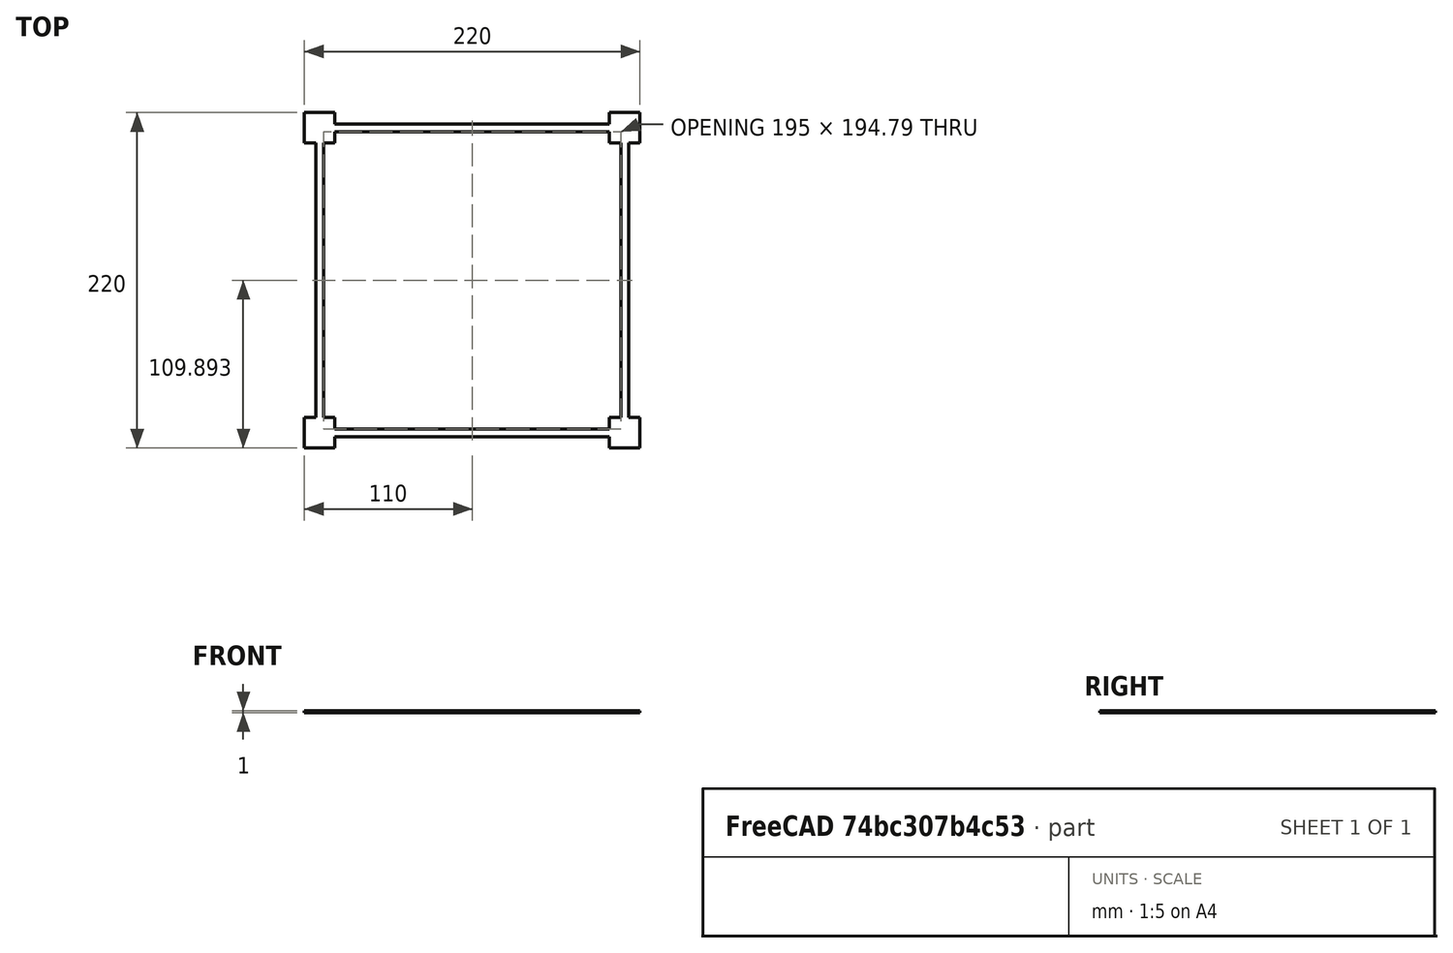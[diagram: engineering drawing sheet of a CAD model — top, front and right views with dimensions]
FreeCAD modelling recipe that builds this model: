
FCSTD DOCUMENT  (FreeCAD 1.1R42131 (Git))
Label: Ender 3 V3 SE Levelling
License: All rights reserved
LicenseURL: https://en.wikipedia.org/wiki/All_rights_reserved
objects: App::Point×1, Sketcher::SketchObject×1, PartDesign::Pad×1, PartDesign::Body×1
note: 6 computed .brp shape members not serialized (recipe doc carries the construction recipe); baked Part::Feature solids carry a one-line shape summary decoded from their .brp

FEATURE [App::Point] Origin001
  Role = Origin
FEATURE [Sketcher::SketchObject] Sketch
  ArcFitTolerance = 1e-06
  AttachmentSupport = -> [Origin]
  ExternalTypes = [0]
  FullyConstrained = false
  MakeInternals = false
  MapMode = 5
  sketch-geometry (36):
    g0: LineSegment StartX=-110 StartY=110 StartZ=0 EndX=-110 EndY=90 EndZ=0
    g1: LineSegment StartX=-110 StartY=90 StartZ=0 EndX=-90 EndY=90 EndZ=0
    g2: LineSegment StartX=-90 StartY=90 StartZ=0 EndX=-90 EndY=110 EndZ=0
    g3: LineSegment StartX=-90 StartY=110 StartZ=0 EndX=-110 EndY=110 EndZ=0
    g4: GeomPoint [constr] X=-100 Y=100 Z=0
    g5: LineSegment StartX=-110 StartY=-90 StartZ=0 EndX=-110 EndY=-110 EndZ=0
    g6: LineSegment StartX=-110 StartY=-110 StartZ=0 EndX=-90 EndY=-110 EndZ=0
    g7: LineSegment StartX=-90 StartY=-110 StartZ=0 EndX=-90 EndY=-90 EndZ=0
    g8: LineSegment StartX=-90 StartY=-90 StartZ=0 EndX=-110 EndY=-90 EndZ=0
    g9: GeomPoint [constr] X=-100 Y=-100 Z=0
    g10: LineSegment StartX=110 StartY=-90 StartZ=0 EndX=110 EndY=-110 EndZ=0
    g11: LineSegment StartX=110 StartY=-110 StartZ=0 EndX=90 EndY=-110 EndZ=0
    g12: LineSegment StartX=90 StartY=-110 StartZ=0 EndX=90 EndY=-90 EndZ=0
    g13: LineSegment StartX=90 StartY=-90 StartZ=0 EndX=110 EndY=-90 EndZ=0
    g14: GeomPoint [constr] X=100 Y=-100 Z=0
    g15: LineSegment StartX=110 StartY=110 StartZ=0 EndX=110 EndY=90 EndZ=0
    g16: LineSegment StartX=110 StartY=90 StartZ=0 EndX=90 EndY=90 EndZ=0
    g17: LineSegment StartX=90 StartY=90 StartZ=0 EndX=90 EndY=110 EndZ=0
    g18: LineSegment StartX=90 StartY=110 StartZ=0 EndX=110 EndY=110 EndZ=0
    g19: GeomPoint [constr] X=100 Y=100 Z=0
    g20: LineSegment StartX=-90 StartY=102.5 StartZ=0 EndX=-90 EndY=97.2852 EndZ=0
    g21: LineSegment StartX=-90 StartY=97.2852 StartZ=0 EndX=90 EndY=97.2852 EndZ=0
    g22: LineSegment StartX=90 StartY=97.2852 StartZ=0 EndX=90 EndY=102.5 EndZ=0
    g23: LineSegment StartX=90 StartY=102.5 StartZ=0 EndX=-90 EndY=102.5 EndZ=0
    g24: LineSegment StartX=-102.5 StartY=-90 StartZ=0 EndX=-97.5 EndY=-90 EndZ=0
    g25: LineSegment StartX=-97.5 StartY=-90 StartZ=0 EndX=-97.5 EndY=90 EndZ=0
    g26: LineSegment StartX=-97.5 StartY=90 StartZ=0 EndX=-102.5 EndY=90 EndZ=0
    g27: LineSegment StartX=-102.5 StartY=90 StartZ=0 EndX=-102.5 EndY=-90 EndZ=0
    g28: LineSegment StartX=-90 StartY=-97.5 StartZ=0 EndX=-90 EndY=-102.5 EndZ=0
    g29: LineSegment StartX=-90 StartY=-102.5 StartZ=0 EndX=90 EndY=-102.5 EndZ=0
    g30: LineSegment StartX=90 StartY=-102.5 StartZ=0 EndX=90 EndY=-97.5 EndZ=0
    g31: LineSegment StartX=90 StartY=-97.5 StartZ=0 EndX=-90 EndY=-97.5 EndZ=0
    g32: LineSegment StartX=97.5 StartY=90 StartZ=0 EndX=97.5 EndY=-90 EndZ=0
    g33: LineSegment StartX=97.5 StartY=-90 StartZ=0 EndX=102.5 EndY=-90 EndZ=0
    g34: LineSegment StartX=102.5 StartY=-90 StartZ=0 EndX=102.5 EndY=90 EndZ=0
    g35: LineSegment StartX=102.5 StartY=90 StartZ=0 EndX=97.5 EndY=90 EndZ=0
  constraints (99):
    c: Coincident(g0,g1)
    c: Coincident(g1,g2)
    c: Coincident(g2,g3)
    c: Coincident(g3,g0)
    c: Vertical(g0)
    c: Vertical(g2)
    c: Horizontal(g1)
    c: Horizontal(g3)
    c: Symmetric(g2,g0,g4)
    c: Coincident(g5,g6)
    c: Coincident(g6,g7)
    c: Coincident(g7,g8)
    c: Coincident(g8,g5)
    c: Vertical(g5)
    c: Vertical(g7)
    c: Horizontal(g6)
    c: Horizontal(g8)
    c: Symmetric(g7,g5,g9)
    c: Coincident(g10,g11)
    c: Coincident(g11,g12)
    c: Coincident(g12,g13)
    c: Coincident(g13,g10)
    c: Vertical(g10)
    c: Vertical(g12)
    c: Horizontal(g11)
    c: Horizontal(g13)
    c: Symmetric(g12,g10,g14)
    c: Coincident(g15,g16)
    c: Coincident(g16,g17)
    c: Coincident(g17,g18)
    c: Coincident(g18,g15)
    c: Vertical(g15)
    c: Vertical(g17)
    c: Horizontal(g16)
    c: Horizontal(g18)
    c: Symmetric(g17,g15,g19)
    c: Distance(g4,g-2) = 100
    c: Equal(g1,g0)
    c: DistanceY(g0,g0) = 20
    c: Distance(g4,g-1) = 100
    c: Equal(g7,g8)
    c: DistanceX(g8,g8) = 20
    c: Equal(g10,g13)
    c: DistanceY(g10,g10) = 20
    c: Equal(g16,g15)
    c: DistanceY(g17,g17) = 20
    c: Distance(g19,g-1) = 100
    c: Distance(g19,g-2) = 100
    c: Distance(g14,g-2) = 100
    c: Distance(g14,g-1) = 100
    c: Distance(g9,g-2) = 100
    c: Distance(g9,g-1) = 100
    c: Coincident(g20,g21)
    c: Coincident(g21,g22)
    c: Coincident(g22,g23)
    c: Coincident(g23,g20)
    c: Vertical(g20)
    c: Vertical(g22)
    c: Horizontal(g21)
    c: Horizontal(g23)
    c: PointOnObject(g20,g2)
    c: PointOnObject(g21,g17)
    c: Coincident(g24,g25)
    c: Coincident(g25,g26)
    c: Coincident(g26,g27)
    c: Coincident(g27,g24)
    c: Horizontal(g24)
    c: Horizontal(g26)
    c: Vertical(g25)
    c: Vertical(g27)
    c: PointOnObject(g24,g8)
    c: PointOnObject(g25,g1)
    c: Distance(g25,g27) = 5
    c: Coincident(g28,g29)
    c: Coincident(g29,g30)
    c: Coincident(g30,g31)
    c: Coincident(g31,g28)
    c: Vertical(g28)
    c: Vertical(g30)
    c: Horizontal(g29)
    c: Horizontal(g31)
    c: PointOnObject(g28,g7)
    c: PointOnObject(g29,g12)
    c: Distance(g31,g29) = 5
    c: Coincident(g32,g33)
    c: Coincident(g33,g34)
    c: Coincident(g34,g35)
    c: Coincident(g35,g32)
    c: Vertical(g32)
    c: Vertical(g34)
    c: Horizontal(g33)
    c: Horizontal(g35)
    c: PointOnObject(g32,g16)
    c: PointOnObject(g33,g13)
    c: Distance(g34,g32) = 5
    c: Distance(g32,g12) = 7.5
    c: DistanceY(g11,g29) = 7.5
    c: DistanceX(g24,g7) = 7.5
    c: DistanceY(g20,g2) = 7.5
FEATURE [PartDesign::Pad] Pad
  Direction = (0,0,1)
  Length = 1
  Length2 = 10
  Profile = -> Sketch
  ReferenceAxis = -> Sketch [N_Axis]
  Refine = true
  SideType = 0
  Suppressed = false
  Type = 0
  Type2 = 0
FEATURE [PartDesign::Body] Body
  AllowCompound = false
  Group = -> [Sketch,Pad]
  Origin = -> Origin
  Tip = -> Pad
